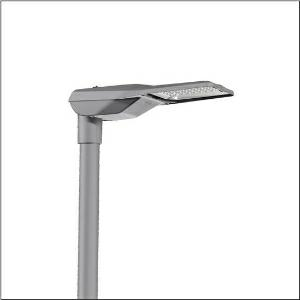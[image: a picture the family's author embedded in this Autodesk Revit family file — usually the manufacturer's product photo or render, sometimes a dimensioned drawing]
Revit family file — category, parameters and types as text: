
# Revit family: streetlight_sl_21_mini___p0_8a_5xe2u33s08hb_bff9
name_source: partatom
category: Lighting Fixtures
units: mm (PartAtom-declared; Revit-internal decimal feet)

## family parameters
Cut with Voids When Loaded = No
Host = Face
Light Source = No
Part Type = Normal
Room Calculation Point = No
Round Connector Dimension = Use Diameter
Shared = No

## types (1)
- --- (1 x LED, 9120 lm, 66 W, 3000K)
    Apparent Load = 66 VA
    CIE Flux Codes = 33 69 96 100 100
    Color Rendering = 70
    Color Temperature = 3000K
    Default Elevation = 1800 mm
    Description = Streetlight SL 21 mini, mast luminaire, primary light control with lens, of PMMA, primary optical cover: cover, of toughened safety glass, transparent, light distribution: P0.8a, light emission: direct distribution, primary light characteristic: asymmetric, installation type: post-top, side-entry, LED, High Power LED, rated luminous flux: 9.120lm, luminous efficacy: 138lm/W, light colour: 730, colour temperature: 3000K, control gear: D4i, control: pre-setting: logarithmic dimming characteristic, flexible luminous flux parameterisation, time-dependent luminous flux control, constant luminous flux control, overheat protection, mains connection: 220..240V, AC, 50/60Hz, start of lifetime: 66W, end of service life: 69W, reduction: 30W, luminaire housing, of diecast aluminium, powder-coated, Siteco® metallic grey (DB 702S), corrosivity category C5 mid according to DIN EN ISO 12944, multi-level sealing system, sealing non-destructively replaceable, inclination adjustable: 0°, 5°, 10°, 15°, please order mast flange separately, length: 628mm, width: 235mm, height: 110mm, mast flange for spigot size: 42mm (side-entry): 5XC10008XM4, 60/48mm (side-entry/post-top): 5XC10108XM2, 76/60mm (side-entry/post-top): 5XC10108XM1, mounting height: 4..8m, Smart Interface above, protection rating (complete): IP66, insulation class (complete): insulation class II (safety insulation), certification: CE, ENEC, ENEC+, VDE, impact resistance: IK10, permissible operating ambient temperature for outdoor applications: -40..+50°C, standard-compliant lighting for roads and squares, packaging unit: 1 piece

Light Distribution: P0.8a
    Height = 110 mm
    Lamp = 1 x LED
    Lamp Light Flux = 9120 lm
    Lamp Power = 66 W
    Lamp count = 1
    Length = 625 mm
    Luminous efficacy = 138 lm/W
    Manufacturer = Siteco
    ModVariant = No
    Model = 5XE2U33S08HB
    Number of Poles = 1
    OnlyDefault = Yes
    Power Factor = 1
    Product Name = Streetlight SL 21 mini | P0.8a
    Product group = mast luminaire | pylon top
    ProductGroupID = 6100
    Protection Class = Protection class II
    Protection Degree = IP 66
    RLX_Detail_Level = 1
    RLX_Emergency_Light_Flux = 0 lm
    RLX_Emergency_Type = 0
    RLX_Emergency_Type_DB = No
    RlxData = <blob elided: 91809 chars, md5=ca0ccb42>
    Socket = socket
    Standby Power = 0 W
    System Light Flux = 9120 lm
    System Power = 66 W
    Type Comments = factory setting: luminous flux: 100 % | dim-lin: 254 | 670 mA
    Type Image = l_1003515.jpg
    URL = http://relux.com
    VarID = @adj_094037
    Voltage = 0 V
    Weight = 0.00 kg
    Width = 234 mm

## geometry (parser evidence)
native form markers: Blend x4, Sweep x11
no freeform markers — native parametric forms only
